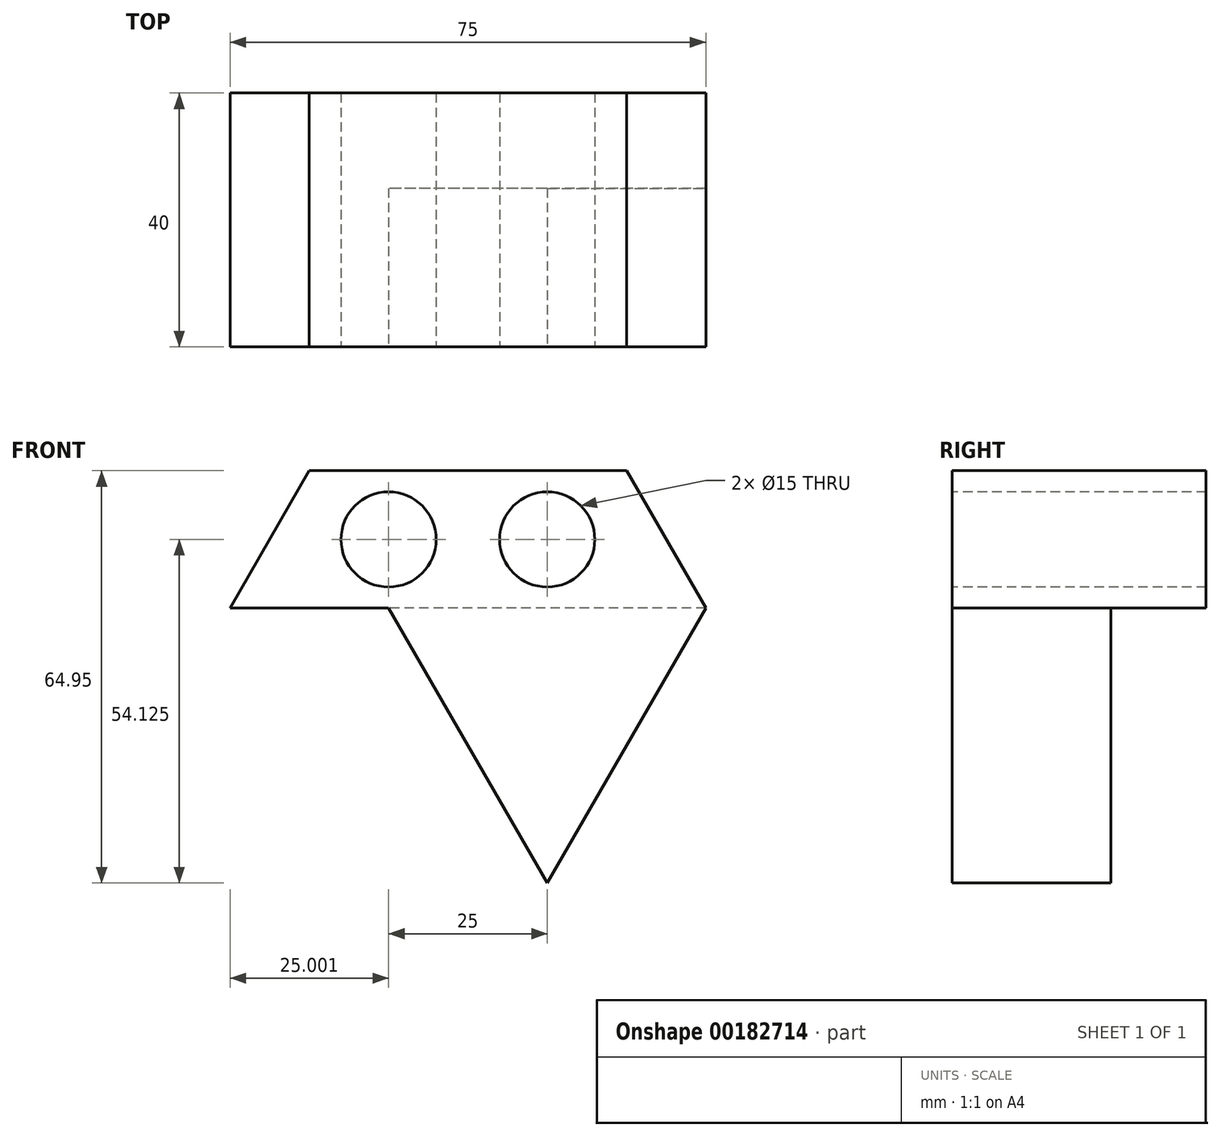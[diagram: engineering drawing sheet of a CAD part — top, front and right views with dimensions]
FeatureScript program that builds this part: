
annotation { "Feature Type Name" : "Feature", "Feature Type Description" : "" }
export const myFeature = defineFeature(function(context is Context, id is Id, definition is map)
    precondition{}
    {
        {
            var Q0;
            Q0=qCreatedBy(makeId("Front.planeOp"),FACE);
            var sketch = newSketch(context, id + "F0", { "sketchPlane" : qUnion([Q0])});
            skLineSegment(sketch, "E0", {"start": v(-52.24, -64.73) * mm, "end": v(-77.24, -21.43) * mm});
            skLineSegment(sketch, "E1", {"start": v(-52.24, -64.73) * mm, "end": v(-27.24, -21.43) * mm});
            skLineSegment(sketch, "E2", {"start": v(-102.24, -21.43) * mm, "end": v(-89.74, 0.22) * mm});
            skLineSegment(sketch, "E3", {"start": v(-39.74, 0.22) * mm, "end": v(-89.74, 0.22) * mm});
            skLineSegment(sketch, "E4", {"start": v(-27.24, -21.43) * mm, "end": v(-39.74, 0.22) * mm});
            skLineSegment(sketch, "E5", {"start": v(-27.24, -21.43) * mm, "end": v(-77.24, -21.43) * mm});
            skLineSegment(sketch, "E6", {"start": v(-27.24, -21.43) * mm, "end": v(-102.24, -21.43) * mm});
            skLineSegment(sketch, "E7", {"start": v(-52.24, -21.43) * mm, "end": v(-52.24, -20.96) * mm});
            skLineSegment(sketch, "E8.trimOffspring", {"start": v(-52.24, -0.25) * mm, "end": v(-52.24, 0.22) * mm});
            skPoint(sketch, "E9", {"position": v(-52.24, -10.6) * mm});
            skPoint(sketch, "E10", {"position": v(-77.24, -10.6) * mm});
            skPoint(sketch, "E11", {"position": v(-95.42, 68.38) * mm});
            skPoint(sketch, "E12.orphan", {"position": v(-95.99, -10.6) * mm});
            skPoint(sketch, "E13.orphan", {"position": v(-77.24, 0.22) * mm});
            skSolve(sketch);
        }
        {
            var Q0;
            Q0=makeQuery(id+"F0.imprint","IMPRINT",FACE,{"disambiguationData":[TD([[makeQuery(id+"F0.imprint","IMPRINT",EDGE,{"derivedFrom":sQuery(id+"F0.wireOp",EDGE,"E0")}),-1.0]])]});
            extrude(context, id + "F1", {"entities" : qUnion([Q0]), "oppositeDirection" : true, "depth" : 25 * mm});
        }
        {
            var Q0;
            Q0=makeQuery(id+"F0.imprint","IMPRINT",FACE,{"disambiguationData":[TD([[makeQuery(id+"F0.imprint","IMPRINT",EDGE,{"derivedFrom":sQuery(id+"F0.wireOp",EDGE,"E2")}),-1.0]])]});
            extrude(context, id + "F2", {"entities" : qUnion([Q0]), "operationType" : NewBodyOperationType.ADD, "oppositeDirection" : true, "depth" : 40 * mm});
        }
        {
            var Q0;
            Q0=sQuery(id+"F0.wireOp",VERTEX,"E9");
            var Q1;
            Q1=makeQuery(id+"F1.opExtrude","SWEPT_BODY",BODY,{"disambiguationData":[OSD([sQuery(id+"F0.wireOp",EDGE,"E0"),sQuery(id+"F0.wireOp",EDGE,"E1"),sQuery(id+"F0.wireOp",EDGE,"E5")])]});
            hole(context, id + "F3", {"style" : HoleStyle.SIMPLE, "endStyle" : HoleEndStyle.THROUGH, "holeDiameter" : 15 * mm, "locations" : qUnion([Q0]), "scope" : qUnion([Q1]), "isTappedThrough" : true});
        }
        {
            var Q0;
            Q0=sQuery(id+"F0.wireOp",VERTEX,"E10");
            var Q1;
            Q1=makeQuery(id+"F1.opExtrude","SWEPT_BODY",BODY,{"disambiguationData":[OSD([sQuery(id+"F0.wireOp",EDGE,"E0"),sQuery(id+"F0.wireOp",EDGE,"E1"),sQuery(id+"F0.wireOp",EDGE,"E5")])]});
            hole(context, id + "F4", {"style" : HoleStyle.SIMPLE, "endStyle" : HoleEndStyle.THROUGH, "holeDiameter" : 15 * mm, "locations" : qUnion([Q0]), "scope" : qUnion([Q1]), "isTappedThrough" : true});
        }
    });
